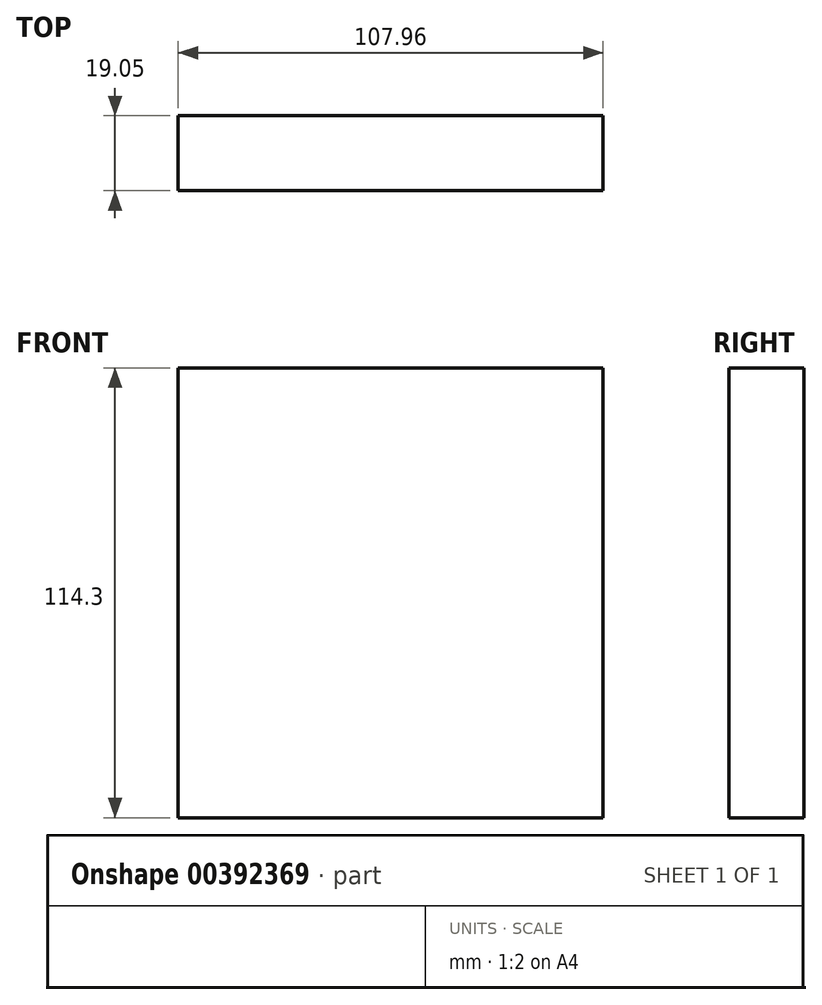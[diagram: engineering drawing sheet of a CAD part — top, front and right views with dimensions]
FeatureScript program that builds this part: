
annotation { "Feature Type Name" : "Feature", "Feature Type Description" : "" }
export const myFeature = defineFeature(function(context is Context, id is Id, definition is map)
    precondition{}
    {
        {
            var Q0;
            Q0=qCreatedBy(makeId("Front.planeOp"),FACE);
            var sketch = newSketch(context, id + "F0", { "sketchPlane" : qUnion([Q0])});
            skLineSegment(sketch, "E0.bottom", {"start": v(-53.97, 0) * mm, "end": v(53.98, 0) * mm});
            skLineSegment(sketch, "E0.top", {"start": v(-53.98, -114.3) * mm, "end": v(53.98, -114.3) * mm});
            skLineSegment(sketch, "E0.left", {"start": v(-53.97, 0) * mm, "end": v(-53.97, -114.3) * mm});
            skLineSegment(sketch, "E0.right", {"start": v(53.98, 0) * mm, "end": v(53.98, -114.3) * mm});
            skSolve(sketch);
        }
        {
            var Q0;
            Q0=makeQuery(id+"F0.imprint","IMPRINT",FACE,{"disambiguationData":[TD([[makeQuery(id+"F0.imprint","IMPRINT",EDGE,{"derivedFrom":sQuery(id+"F0.wireOp",EDGE,"E0.bottom")}),-1.0]])]});
            extrude(context, id + "F1", {"entities" : qUnion([Q0]), "depth" : 19.05 * mm});
        }
    });
